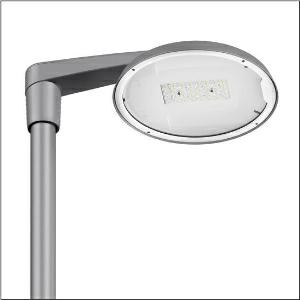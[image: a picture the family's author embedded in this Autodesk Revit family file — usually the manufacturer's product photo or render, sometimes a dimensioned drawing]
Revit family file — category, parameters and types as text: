
# Revit family: dl_r__50_iq_mini___st0_5a_5xa248b41f08ge_47f6
name_source: partatom
category: Lighting Fixtures
units: mm (PartAtom-declared; Revit-internal decimal feet)

## family parameters
Cut with Voids When Loaded = No
Host = Face
Light Source = No
Part Type = Normal
Room Calculation Point = No
Round Connector Dimension = Use Diameter
Shared = No

## types (1)
- --- (1 x LED, 5190 lm, 31.2 W, 4000K)
    Apparent Load = 31 VA
    CIE Flux Codes = 41 75 97 100 100
    Color Rendering = 70
    Color Temperature = 4000K
    Default Elevation = 1800 mm
    Description = DL® 50 iQ mini, mast luminaire, primary light control with lens, of PMMA, primary optical cover: cover, of toughened safety glass, transparent, light distribution: ST0.5a, light emission: direct distribution, primary light characteristic: asymmetric, installation type: side-entry, post-top, LED, High Power LED, rated luminous flux: 5.190lm, luminous efficacy: 166lm/W, light colour: 740, colour temperature: 4000K, control: optimised constant luminous flux control (CLO 2.0), Desk-Remote (wireless, voltage-free reading and setting of iQ features in the workshop via application-optimized NFC function/RFID function), Light-Fading, Smart-Wire, Night-Set, Lumen-Switch, Temp-Guard, Auto-Match, Street-Remote, mains connection: 230..240V, AC, 50/60Hz, connection cable pre-assembled, cable length: 6,5m, start of lifetime: 31W, end of service life: 32W, reduction: 15W, luminaire housing, of diecast aluminium, powder-coated, Siteco® metallic grey (DB 702S), inclination adjustable: 0°, 5°, 10° (post-top) | 0°, -5°, -10°, -15° (side-entry), please order mast post-top element or mast side-entry element separately, diameter: 500mm, height: 115mm, post-top: for spigot size d x l = 76 x 100mm; with reducer (optional accessory) 60 x 100mm | side-entry: for spigot size d x l = 60 x 100mm; with reducer (optional accessory) 42 x 100mm, protection rating (complete): IP66, insulation class (complete): insulation class II (safety insulation), certification: CE, ENEC, VDE, impact resistance: IK08, permissible operating ambient temperature for outdoor applications: -25..+40°C, standard-compliant lighting for roads and squares, packaging unit: 1 piece

Light Distribution: ST0.5a
    Height = 115 mm
    Lamp = 1 x LED
    Lamp Light Flux = 5190 lm
    Lamp Power = 31.2 W
    Lamp count = 1
    Length = 500 mm
    Luminous efficacy = 166 lm/W
    Manufacturer = Siteco
    ModVariant = No
    Model = 5XA248B41F08GE
    Number of Poles = 1
    OnlyDefault = Yes
    Power Factor = 1
    Product Name = DL® 50 iQ mini | ST0.5a
    Product group = mast luminaire | pylon top
    ProductGroupID = 6100
    Protection Class = Protection class II
    Protection Degree = IP 66
    RLX_Detail_Level = 1
    RLX_Emergency_Light_Flux = 0 lm
    RLX_Emergency_Type = 0
    RLX_Emergency_Type_DB = No
    RlxData = <blob elided: 126981 chars, md5=083e2ef4>
    Socket = socket
    Standby Power = 0 W
    System Light Flux = 5190 lm
    System Power = 31 W
    Type Comments = factory setting: luminous flux: 100 % | dim-lin: 254 | 325 mA
    Type Image = l_1251794.jpg
    URL = http://relux.com
    VarID = @adj_092631
    Voltage = 0 V
    Weight = 0.00 kg
    Width = 0 mm  [stored 0 ft]

note: [stored X ft] marks values corroborated as IEEE doubles in the binary element streams (Revit-internal decimal feet)

## geometry (parser evidence)
native form markers: Blend x4, Sweep x11
no freeform markers — native parametric forms only
